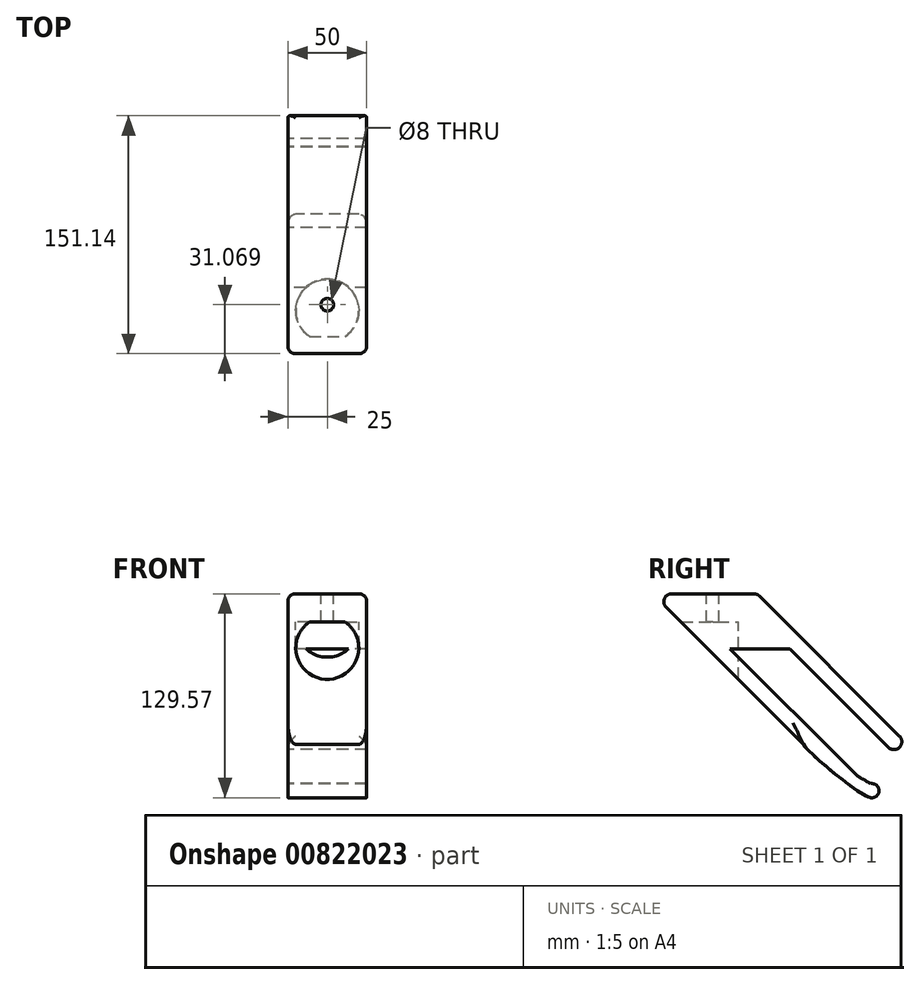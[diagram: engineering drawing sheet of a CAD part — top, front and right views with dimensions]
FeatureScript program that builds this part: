
annotation { "Feature Type Name" : "Feature", "Feature Type Description" : "" }
export const myFeature = defineFeature(function(context is Context, id is Id, definition is map)
    precondition{}
    {
        {
            var Q0;
            Q0=qCreatedBy(makeId("Right.planeOp"),FACE);
            var sketch = newSketch(context, id + "F0", { "sketchPlane" : qUnion([Q0])});
            skLineSegment(sketch, "E0", {"start": v(-33.05, 0) * mm, "end": v(33.23, 0) * mm});
            skLineSegment(sketch, "E1", {"start": v(33.23, 0) * mm, "end": v(132.23, -99) * mm});
            skLineSegment(sketch, "E2", {"start": v(132.23, -99) * mm, "end": v(118.08, -99) * mm});
            skLineSegment(sketch, "E3", {"start": v(118.08, -99) * mm, "end": v(54.09, -35) * mm});
            skLineSegment(sketch, "E4", {"start": v(54.09, -35) * mm, "end": v(16.09, -35) * mm});
            skLineSegment(sketch, "E5", {"start": v(16.09, -35) * mm, "end": v(106.16, -125.07) * mm});
            skLineSegment(sketch, "E6", {"start": v(106.16, -125.07) * mm, "end": v(62.6, -95.66) * mm});
            skLineSegment(sketch, "E7", {"start": v(62.6, -95.66) * mm, "end": v(-33.05, 0) * mm});
            skCircle(sketch, "E8", {"center": v(106.16, -125.07) * mm, "radius": 4.5 * mm});
            skFitSpline(sketch, "E9", {"points": [v(62.6, -95.66) * mm, v(105.65, -129.54) * mm], "startDerivative": vector(6.97, -14.48) * mm, "endDerivative": vector(15.12, 2.11) * mm});
            skFitSpline(sketch, "E10", {"points": [v(94.68, -113.59) * mm, v(100.9, -118.01) * mm, v(105.28, -120.65) * mm], "startDerivative": vector(15.22, -15.22) * mm, "endDerivative": vector(9.57, -5.08) * mm});
            skLineSegment(sketch, "E11", {"start": v(99.76, -66.53) * mm, "end": v(31.85, -134.43) * mm, "construction": true});
            skSolve(sketch);
        }
        {
            var Q0;
            Q0 = qSketchRegion(id + "F0", true);
            var Q1;
            {var subQ0=sQuery(id+"F0.wireOp",EDGE,"E6");var subQ1=sQuery(id+"F0.wireOp",EDGE,"E5");var subQ2=makeQuery(id+"F0.imprint","INTERSECT",VERTEX,{"derivedFrom":[subQ1,subQ0]});Q1=makeQuery(id+"F0.imprint","IMPRINT",FACE,{"disambiguationData":[TD([[makeQuery(id+"F0.imprint","IMPRINT",EDGE,{"disambiguationData":[TD([[subQ2,1.0]])],"derivedFrom":subQ1}),-1.0]])]});}
            extrude(context, id + "F1", {"entities" : qUnion([Q0, Q1]), "depth" : 50 * mm, "offsetDistance" : 25 * mm});
        }
        {
            var Q0;
            Q0=makeQuery(id+"F1.opExtrude","CAP_EDGE",EDGE,{"disambiguationData":[OSD([sQuery(id+"F0.wireOp",EDGE,"E1")])],"isStart":false});
            var Q1;
            Q1=makeQuery(id+"F1.opExtrude","CAP_EDGE",EDGE,{"disambiguationData":[OSD([sQuery(id+"F0.wireOp",EDGE,"E1")])],"isStart":true});
            var Q2;
            Q2=makeQuery(id+"F1.opExtrude","CAP_EDGE",EDGE,{"disambiguationData":[OSD([sQuery(id+"F0.wireOp",EDGE,"E7")])],"isStart":true});
            var Q3;
            Q3=makeQuery(id+"F1.opExtrude","CAP_EDGE",EDGE,{"disambiguationData":[OSD([sQuery(id+"F0.wireOp",EDGE,"E7")])],"isStart":false});
            var Q4;
            Q4=makeQuery(id+"F1.opExtrude","SWEPT_EDGE",EDGE,{"disambiguationData":[OSD([sQuery(id+"F0.wireOp",EDGE,"E0"),sQuery(id+"F0.wireOp",EDGE,"E1")])]});
            var Q5;
            Q5=makeQuery(id+"F1.opExtrude","CAP_EDGE",EDGE,{"disambiguationData":[OSD([sQuery(id+"F0.wireOp",EDGE,"E0")])],"isStart":false});
            var Q6;
            Q6=makeQuery(id+"F1.opExtrude","CAP_EDGE",EDGE,{"disambiguationData":[OSD([sQuery(id+"F0.wireOp",EDGE,"E0")])],"isStart":true});
            var Q7;
            Q7=makeQuery(id+"F1.opExtrude","SWEPT_EDGE",EDGE,{"disambiguationData":[OSD([sQuery(id+"F0.wireOp",EDGE,"E0"),sQuery(id+"F0.wireOp",EDGE,"E7")])]});
            var Q8;
            Q8=makeQuery(id+"F1.opExtrude","SWEPT_EDGE",EDGE,{"disambiguationData":[OSD([sQuery(id+"F0.wireOp",EDGE,"E1"),sQuery(id+"F0.wireOp",EDGE,"E2")])]});
            var Q9;
            Q9=makeQuery(id+"F1.opExtrude","SWEPT_EDGE",EDGE,{"disambiguationData":[OSD([sQuery(id+"F0.wireOp",EDGE,"E2"),sQuery(id+"F0.wireOp",EDGE,"E3")])]});
            fillet(context, id + "F2", {"entities" : qUnion([Q0, Q1, Q2, Q3, Q4, Q5, Q6, Q7, Q8, Q9]), "radius" : 5 * mm, "tangentPropagation" : true, "allowEdgeOverflow" : false});
        }
        {
            var Q0;
            Q0=makeQuery(id+"F1.opExtrude","SWEPT_FACE",FACE,{"disambiguationData":[OSD([sQuery(id+"F0.wireOp",EDGE,"E0")])]});
            var sketch = newSketch(context, id + "F3", { "sketchPlane" : qUnion([Q0])});
            skLineSegment(sketch, "E12", {"start": v(45, -20.98) * mm, "end": v(5, 31.16) * mm, "construction": true});
            skLineSegment(sketch, "E13", {"start": v(5, -20.98) * mm, "end": v(45, 31.16) * mm, "construction": true});
            skPoint(sketch, "E14", {"position": v(25, 5.09) * mm});
            skSolve(sketch);
        }
        {
            var Q0;
            Q0=sQuery(id+"F3.wireOp",VERTEX,"E14");
            var Q1;
            Q1=makeQuery(id+"F1.opExtrude","SWEPT_BODY",BODY,{"disambiguationData":[OSD([sQuery(id+"F0.wireOp",EDGE,"E0"),sQuery(id+"F0.wireOp",EDGE,"E1"),sQuery(id+"F0.wireOp",EDGE,"E2"),sQuery(id+"F0.wireOp",EDGE,"E3"),sQuery(id+"F0.wireOp",EDGE,"E4"),sQuery(id+"F0.wireOp",EDGE,"E5"),sQuery(id+"F0.wireOp",EDGE,"E7"),sQuery(id+"F0.wireOp",EDGE,"E8"),sQuery(id+"F0.wireOp",EDGE,"E9"),sQuery(id+"F0.wireOp",EDGE,"E10")])]});
            hole(context, id + "F4", {"style" : HoleStyle.SIMPLE, "endStyle" : HoleEndStyle.THROUGH, "holeDiameter" : 8 * mm, "majorDiameter" : 5 * mm, "isTappedThrough" : true, "tappedDepth" : 12 * mm, "tapClearance" : 3, "locations" : qUnion([Q0]), "scope" : qUnion([Q1])});
        }
        {
            var Q0;
            Q0=makeQuery(id+"F1.opExtrude","SWEPT_FACE",FACE,{"disambiguationData":[OSD([sQuery(id+"F0.wireOp",EDGE,"E4")])]});
            var sketch = newSketch(context, id + "F5", { "sketchPlane" : qUnion([Q0])});
            skCircle(sketch, "E15", {"center": v(25, -1.37) * mm, "radius": 20 * mm});
            skSolve(sketch);
        }
        {
            var Q0;
            Q0 = qSketchRegion(id + "F5", true);
            extrude(context, id + "F6", {"entities" : qUnion([Q0]), "operationType" : NewBodyOperationType.REMOVE, "endBound" : BoundingType.THROUGH_ALL, "depth" : 17 * mm, "offsetDistance" : 25 * mm});
        }
        {
            var Q0;
            Q0 = qSketchRegion(id + "F5", true);
            extrude(context, id + "F7", {"entities" : qUnion([Q0]), "operationType" : NewBodyOperationType.REMOVE, "oppositeDirection" : true, "depth" : 17 * mm, "offsetDistance" : 25 * mm});
        }
    });
